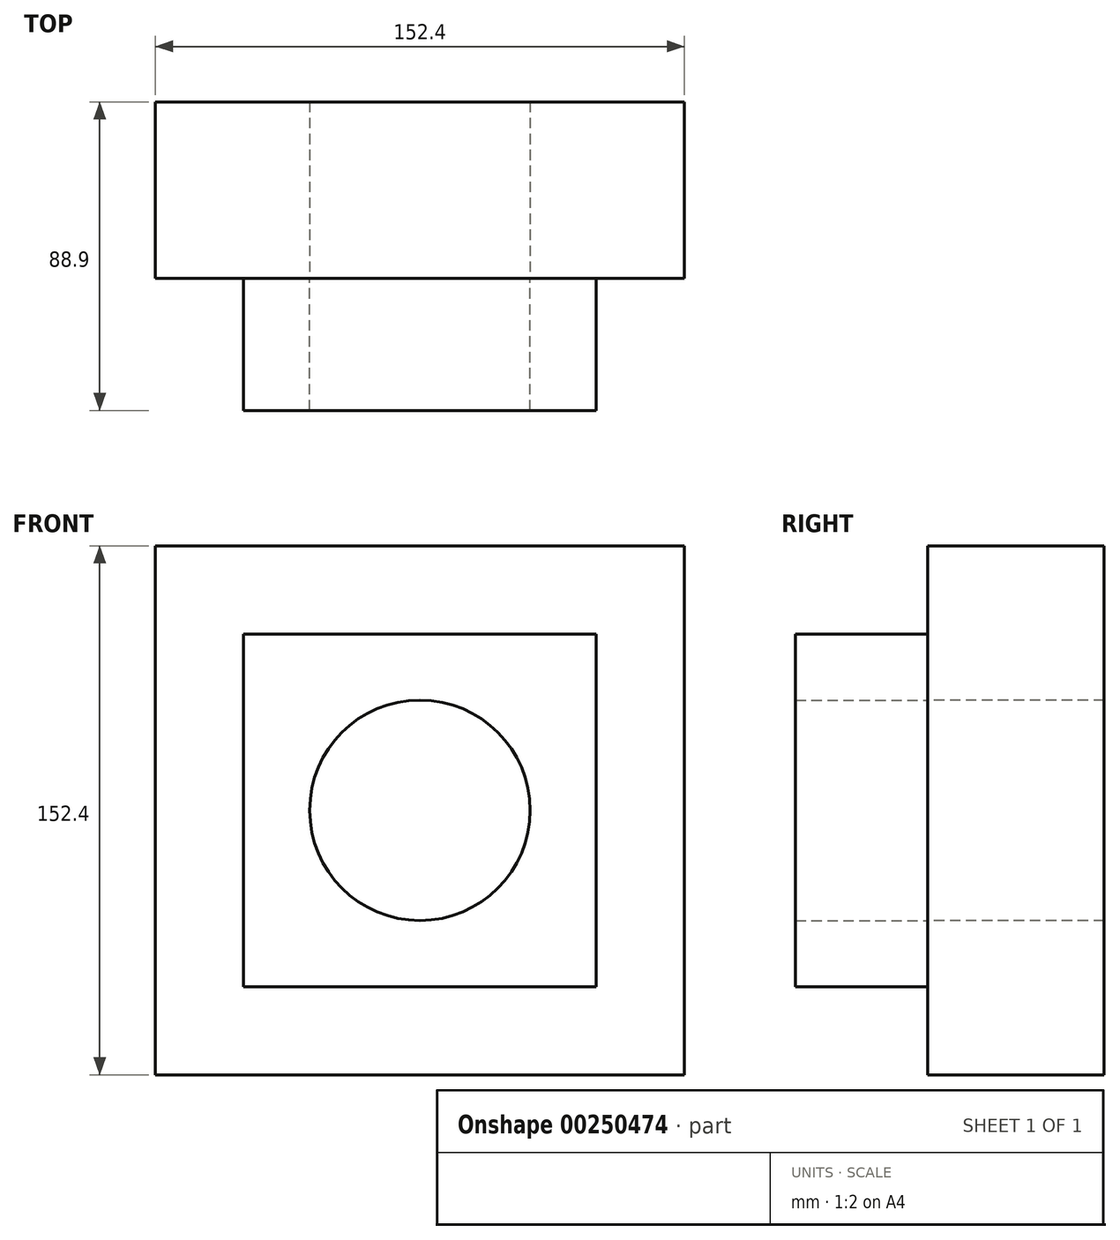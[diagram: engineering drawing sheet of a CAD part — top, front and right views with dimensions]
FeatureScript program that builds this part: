
annotation { "Feature Type Name" : "Feature", "Feature Type Description" : "" }
export const myFeature = defineFeature(function(context is Context, id is Id, definition is map)
    precondition{}
    {
        {
            var Q0;
            Q0=qCreatedBy(makeId("Front.planeOp"),FACE);
            var sketch = newSketch(context, id + "F0", { "sketchPlane" : qUnion([Q0])});
            skCircle(sketch, "E0", {"center": v(0, 0) * mm, "radius": 31.75 * mm});
            skLineSegment(sketch, "E1.bottom", {"start": v(-50.8, 50.8) * mm, "end": v(50.8, 50.8) * mm});
            skLineSegment(sketch, "E1.top", {"start": v(-50.8, -50.8) * mm, "end": v(50.8, -50.8) * mm});
            skLineSegment(sketch, "E1.left", {"start": v(-50.8, 50.8) * mm, "end": v(-50.8, -50.8) * mm});
            skLineSegment(sketch, "E1.right", {"start": v(50.8, 50.8) * mm, "end": v(50.8, -50.8) * mm});
            skLineSegment(sketch, "E2.bottom", {"start": v(-76.2, 76.2) * mm, "end": v(76.2, 76.2) * mm});
            skLineSegment(sketch, "E2.top", {"start": v(-76.2, -76.2) * mm, "end": v(76.2, -76.2) * mm});
            skLineSegment(sketch, "E2.left", {"start": v(-76.2, 76.2) * mm, "end": v(-76.2, -76.2) * mm});
            skLineSegment(sketch, "E2.right", {"start": v(76.2, 76.2) * mm, "end": v(76.2, -76.2) * mm});
            skSolve(sketch);
        }
        {
            var Q0;
            Q0=makeQuery(id+"F0.imprint","IMPRINT",FACE,{"disambiguationData":[TD([[makeQuery(id+"F0.imprint","IMPRINT",EDGE,{"derivedFrom":sQuery(id+"F0.wireOp",EDGE,"E0")}),-1.0]])]});
            extrude(context, id + "F1", {"entities" : qUnion([Q0]), "depth" : 38.1 * mm});
        }
        {
            var Q0;
            Q0=makeQuery(id+"F0.imprint","IMPRINT",FACE,{"disambiguationData":[TD([[makeQuery(id+"F0.imprint","IMPRINT",EDGE,{"derivedFrom":sQuery(id+"F0.wireOp",EDGE,"E1.bottom")}),1.0]])]});
            var Q1;
            Q1=makeQuery(id+"F0.imprint","IMPRINT",FACE,{"disambiguationData":[TD([[makeQuery(id+"F0.imprint","IMPRINT",EDGE,{"derivedFrom":sQuery(id+"F0.wireOp",EDGE,"E0")}),-1.0]])]});
            extrude(context, id + "F2", {"entities" : qUnion([Q0, Q1]), "oppositeDirection" : true, "depth" : 50.8 * mm});
        }
    });
